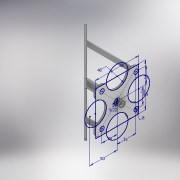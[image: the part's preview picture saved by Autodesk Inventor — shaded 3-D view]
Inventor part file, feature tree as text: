
AUTODESK INVENTOR PART (.ipt)
format: ipt  version: 2017 (Build 210142000, 142)  size: 246,272 bytes
history: native  units: mm
features: extrude x8, sketch x2, chamfer x1, fillet x1
ambient origin geometry x8: Origin, YZ Plane, XZ Plane, XY Plane, X Axis, Y Axis, Z Axis, Center Point
bodies: Solid1 (feature_tree)
feature tree (12):
  extrude  "Extrusion1"  Depth=10.0mm TaperAngle=45.0deg
  chamfer  "Chamfer1"  Distance=4.0mm
  sketch  "Sketch2"  dims[d8=50.0mm d10=4.0mm d11=5.0mm d12=100.0mm d13=0.0mm d14=3.0mm d15=30.0mm d16=30.0mm d17=35.0mm d18=28.0mm d19=8.0mm d20=3.0mm d21=0.0mm d22=5.0mm d23=0.0mm d24=10.0mm d25=3.0mm d26=45.0deg d27=100.0mm d28=80.0mm d29=80.0mm d32=5.0mm d33=0.0mm d34=8.0mm d35=9.22mm d38=40.0mm d39=10.0mm d40=0.0mm d41=8.25mm d42=0.0mm d43=6.22mm d44=0.0mm]
  extrude  "Extrusion2"  Depth=6.22mm
  extrude  "Extrusion3"  Depth=100.0mm TaperAngle=0.0deg
  extrude  "Extrusion4"  Depth=3.0mm
  extrude  "Extrusion5"  Depth=6.22mm
  fillet  "Fillet2"  Radius=30.0mm
  extrude  "Extrusion7"  Depth=35.0mm
  extrude  "Extrusion8"  Depth=6.22mm
  extrude  "Extrusion9"  Depth=8.0mm
  sketch  "Sketch1"  dims[d3=100.0mm d4=0.0mm d5=10.0mm d6=2.0mm d7=45.0deg]
